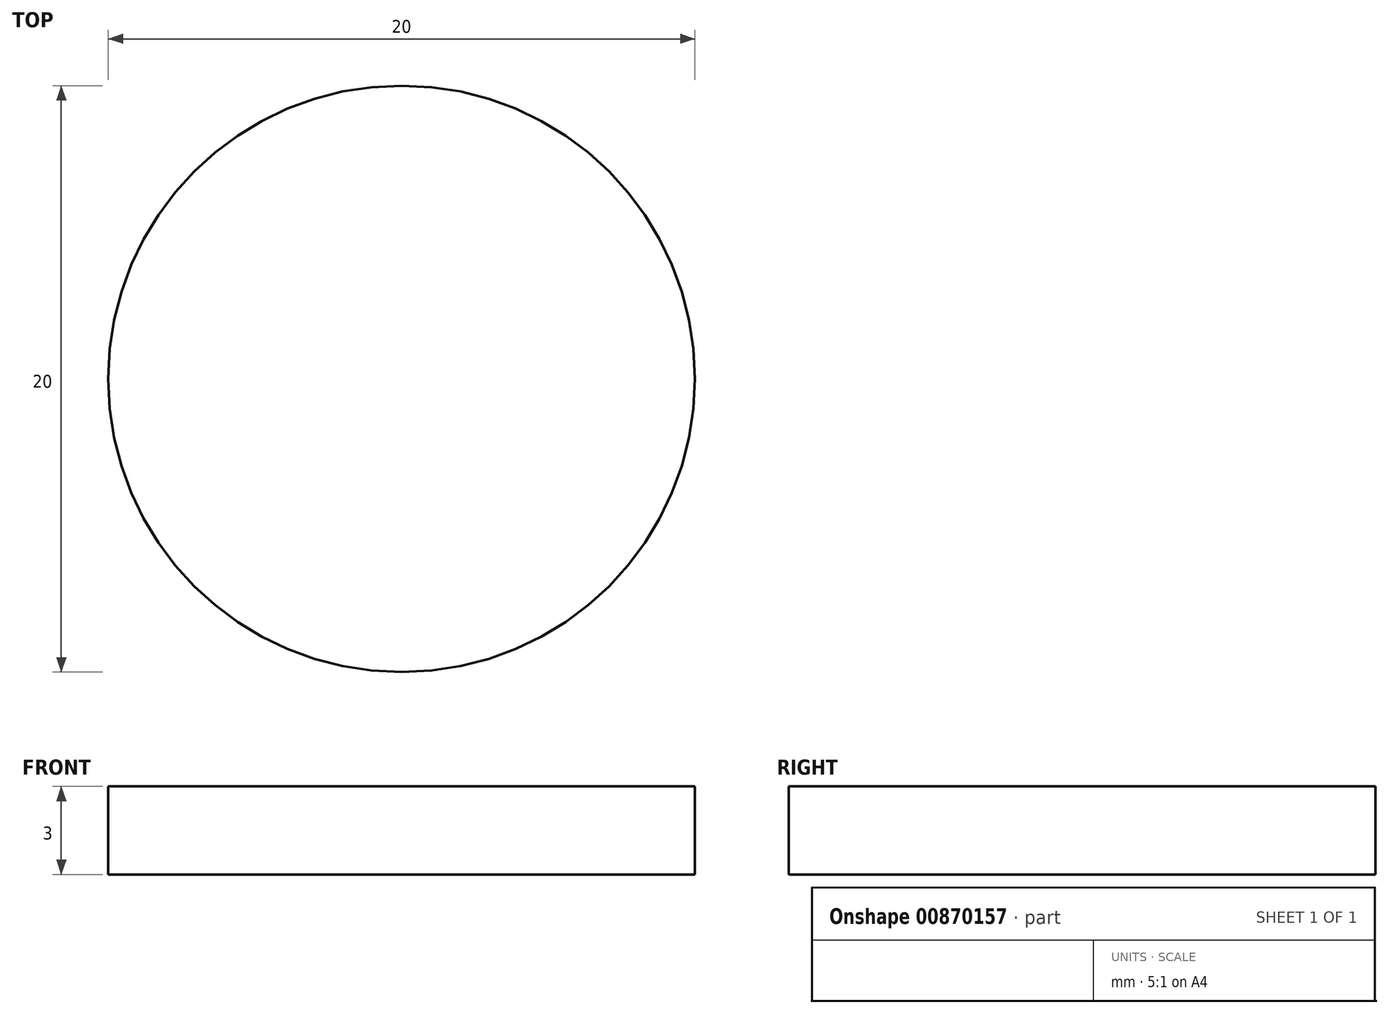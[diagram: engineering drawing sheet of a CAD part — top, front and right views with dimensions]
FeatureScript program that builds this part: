
annotation { "Feature Type Name" : "Feature", "Feature Type Description" : "" }
export const myFeature = defineFeature(function(context is Context, id is Id, definition is map)
    precondition{}
    {
        {
            var Q0;
            Q0=qCreatedBy(makeId("Top.planeOp"),FACE);
            var sketch = newSketch(context, id + "F0", { "sketchPlane" : qUnion([Q0])});
            skCircle(sketch, "E0", {"center": v(0, 0) * mm, "radius": 10 * mm});
            skSolve(sketch);
        }
        {
            var Q0;
            Q0 = qSketchRegion(id + "F0", true);
            extrude(context, id + "F1", {"entities" : qUnion([Q0]), "depth" : 3 * mm, "offsetDistance" : 25.4 * mm});
        }
    });
